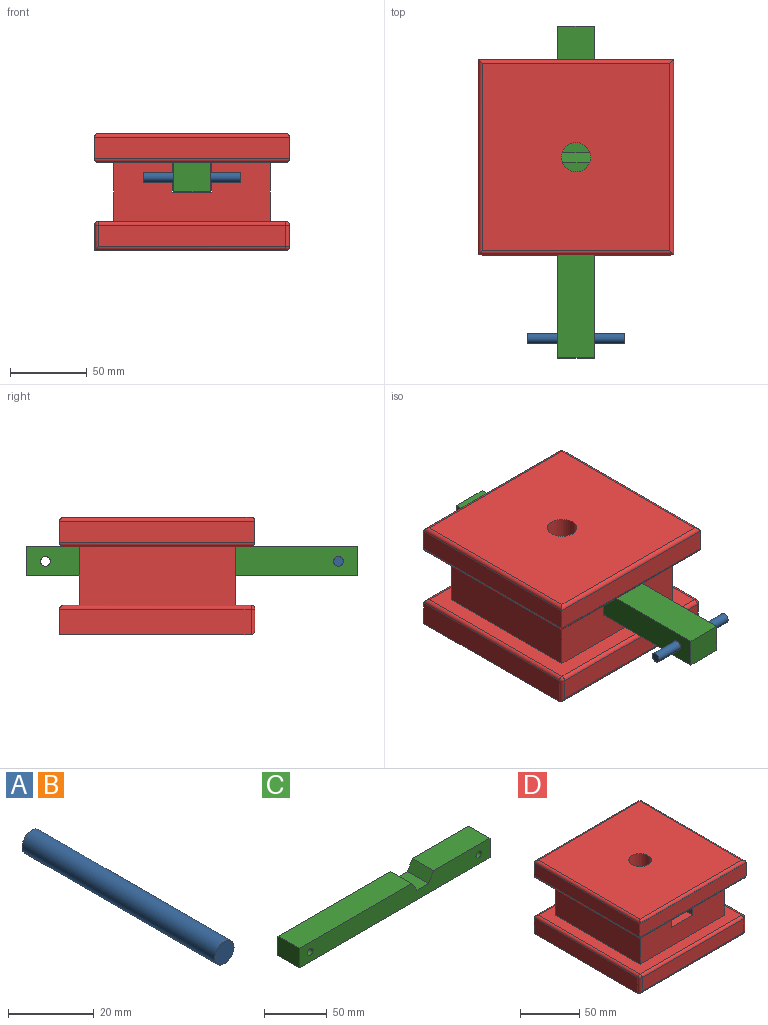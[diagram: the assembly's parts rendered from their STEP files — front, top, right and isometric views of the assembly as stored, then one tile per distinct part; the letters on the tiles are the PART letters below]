
ASSEMBLY  parts=4 mates=2
PART A: 3 faces, bbox 6.4x63.5x6.4 mm
  f0: cylinder r=3.17mm len=63.5mm, axis (0,-1,0), area 1266.8mm2, adj f1,f2
  f1: plane 6.35x6.35mm, normal (0,1,0), area 31.7mm2, adj f0
  f2: plane 6.35x6.35mm, normal (0,-1,0), area 31.7mm2, adj f0
PART B: same geometry as A
PART C: 12 faces, bbox 215.9x23.8x19.1 mm
  f0: plane 23.81x12.7mm, normal (0,0,1), area 302.4mm2, adj f1,f7,f8,f9
  f1: plane 23.81x9.53mm, normal (0.83,0,0.55), area 272.6mm2, adj f0,f2,f8,f9
  f2: plane 127x23.81mm, normal (0,0,1), area 3024.2mm2, adj f1,f3,f8,f9
  f3: plane 23.81x19.05mm, normal (-1,0,0), area 453.6mm2, adj f2,f4,f8,f9
  f4: plane 215.9x23.81mm, normal (0,0,-1), area 5141.1mm2, adj f3,f5,f8,f9
  f5: plane 23.81x19.05mm, normal (1,0,0), area 453.6mm2, adj f4,f6,f8,f9
  f6: plane 63.5x23.81mm, normal (0,0,1), area 1512.1mm2, adj f5,f7,f8,f9
  f7: plane 23.81x9.53mm, normal (-0.83,0,0.55), area 272.6mm2, adj f0,f6,f8,f9
  f8: plane 215.9x19.05mm, normal (0,-1,0), area 3868.1mm2, adj f0,f1,f2,f3,f4,f5,f6,f7
  f9: plane 215.9x19.05mm, normal (0,1,0), area 3868.1mm2, adj f0,f1,f2,f3,f4,f5,f6,f7
  f10: cylinder r=3.17mm len=23.81mm, axis (0,-1,0), area 475mm2, adj f8,f9
  f11: cylinder r=3.17mm len=23.81mm, axis (0,-1,0), area 475mm2, adj f8,f9
PART D: 41 faces, bbox 127x127x76.2 mm
  f0: plane 101.6x38.1mm, normal (0,1,0), area 3387.1mm2, adj f1,f8,f9,f15,f16,f17,f18
  f1: plane 121.92x121.92mm, normal (0,0,1), area 4541.9mm2, adj f0,f7,f8,f9,f28,f32,f35,f36
  f2: plane 121.92x13.97mm, normal (1,0,0), area 1703.2mm2, adj f34,f35,f39,f40
  f3: plane 124.46x16.51mm, normal (0,1,0), area 2054.8mm2, adj f4,f6,f36,f40
  f4: plane 124.46x16.51mm, normal (-1,0,0), area 2054.8mm2, adj f3,f6,f30,f32
  f5: plane 121.92x13.97mm, normal (0,-1,0), area 1703.2mm2, adj f28,f30,f33,f34
  f6: plane 124.46x124.46mm, normal (0,0,-1), area 15490.3mm2, adj f3,f4,f33,f39
  f7: plane 101.6x38.1mm, normal (0,-1,0), area 3387.1mm2, adj f1,f8,f9,f15,f16,f17,f18
  f8: plane 101.6x38.1mm, normal (1,0,0), area 3871mm2, adj f0,f1,f7,f15
  f9: plane 101.6x38.1mm, normal (-1,0,0), area 3871mm2, adj f0,f1,f7,f15
  f10: plane 127x13.97mm, normal (1,0,0), area 1774.2mm2, adj f11,f13,f20,f24
  f11: plane 127x13.97mm, normal (0,1,0), area 1774.2mm2, adj f10,f12,f22,f26
  f12: plane 127x13.97mm, normal (-1,0,0), area 1774.2mm2, adj f11,f13,f23,f27
  f13: plane 127x13.97mm, normal (0,-1,0), area 1774.2mm2, adj f10,f12,f21,f25
  f14: plane 121.92x121.92mm, normal (0,0,1), area 14579.5mm2, adj f19,f20,f21,f22,f23
  f15: plane 121.92x121.92mm, normal (0,0,-1), area 6837.5mm2, adj f0,f7,f8,f9,f16,f18,f19,f24
  f16: plane 101.6x19.05mm, normal (1,0,0), area 1935.5mm2, adj f0,f7,f15,f17
  f17: plane 101.6x25.4mm, normal (0,0,1), area 2580.6mm2, adj f0,f7,f16,f18
  f18: plane 101.6x19.05mm, normal (-1,0,0), area 1935.5mm2, adj f0,f7,f15,f17
  f19: cylinder r=9.53mm len=19.05mm, axis (0,0,1), area 1140.1mm2, adj f14,f15
  f20: cylinder r=2.54mm len=127mm, axis (0,-1,0), area 499.3mm2, adj f10,f14,f21,f22
  f21: cylinder r=2.54mm len=127mm, axis (-1,0,0), area 499.3mm2, adj f13,f14,f20,f23
  f22: cylinder r=2.54mm len=127mm, axis (1,0,0), area 499.3mm2, adj f11,f14,f20,f23
  f23: cylinder r=2.54mm len=127mm, axis (0,1,0), area 499.3mm2, adj f12,f14,f21,f22
  f24: cylinder r=2.54mm len=127mm, axis (0,1,0), area 499.3mm2, adj f10,f15,f25,f26
  f25: cylinder r=2.54mm len=127mm, axis (1,0,0), area 499.3mm2, adj f13,f15,f24,f27
  f26: cylinder r=2.54mm len=127mm, axis (-1,0,0), area 499.3mm2, adj f11,f15,f24,f27
  f27: cylinder r=2.54mm len=127mm, axis (0,-1,0), area 499.3mm2, adj f12,f15,f25,f26
  f28: cylinder r=2.54mm len=121.92mm, axis (-1,0,0), area 486.4mm2, adj f1,f5,f29,f31
  f29: sphere r=2.54mm, area 10.1mm2, adj f28,f30,f32
  f30: cylinder r=2.54mm len=16.51mm, axis (0,0,-1), area 62.2mm2, adj f4,f5,f29,f33
  f31: sphere r=2.54mm, area 10.1mm2, adj f28,f34,f35
  f32: cylinder r=2.54mm len=124.46mm, axis (0,1,0), area 492.9mm2, adj f1,f4,f29,f36
  f33: cylinder r=2.54mm len=124.46mm, axis (1,0,0), area 492.9mm2, adj f5,f6,f30,f37
  f34: cylinder r=2.54mm len=13.97mm, axis (0,0,1), area 55.7mm2, adj f2,f5,f31,f37
  f35: cylinder r=2.54mm len=121.92mm, axis (0,-1,0), area 486.4mm2, adj f1,f2,f31,f38
  f36: cylinder r=2.54mm len=124.46mm, axis (1,0,0), area 492.9mm2, adj f1,f3,f32,f38
  f37: sphere r=2.54mm, area 10.1mm2, adj f33,f34,f39
  f38: sphere r=2.54mm, area 10.1mm2, adj f35,f36,f40
  f39: cylinder r=2.54mm len=124.46mm, axis (0,1,0), area 492.9mm2, adj f2,f6,f37,f40
  f40: cylinder r=2.54mm len=16.51mm, axis (0,0,-1), area 62.2mm2, adj f2,f3,f38,f39
PLACE A rot(axis=(0,0,1),90deg) t=(-66.55,42.48,72.65)mm
PLACE B rot(axis=(0,0,1),90deg) t=(-68.21,198.41,72.65)mm
PLACE C rot(axis=(0,0,1),90deg) t=(-86.42,4.46,118.39)mm
PLACE D t=(-11.01,32,19.43)mm fixed
MATE slider A.f0 <-> C.f10  axis (1,0,0) through (-10.99,-85.83,67.06)mm
MATE slider C.f5 <-> D.f0  axis (0,1,0) through (0.89,117.37,57.53)mm
